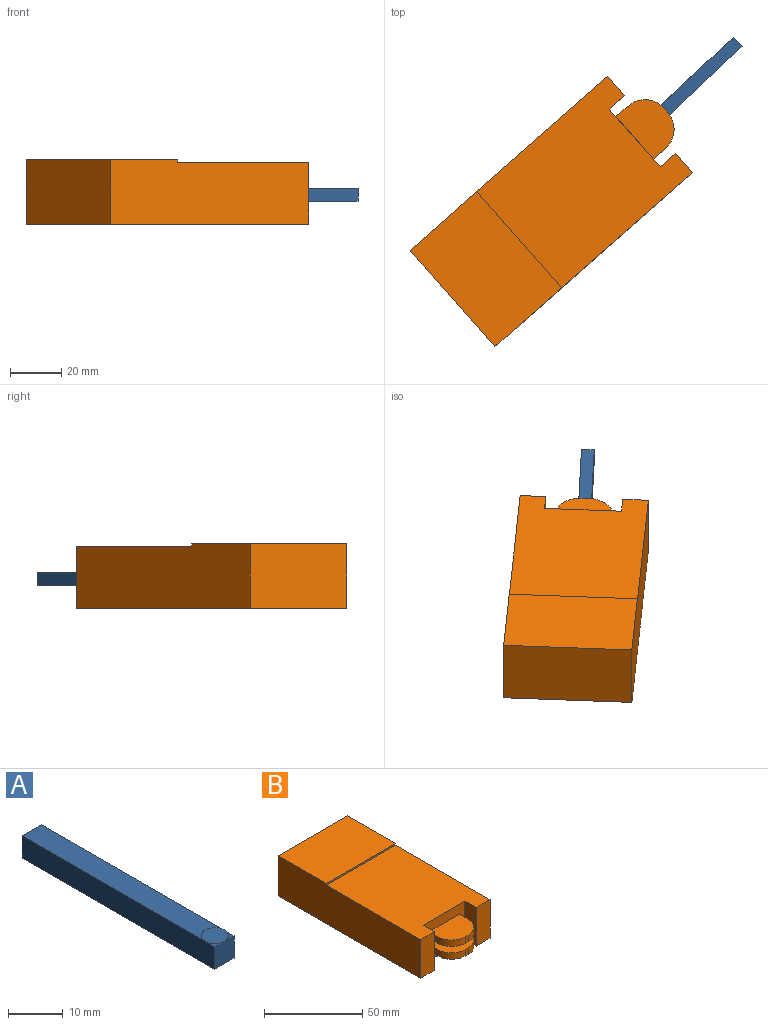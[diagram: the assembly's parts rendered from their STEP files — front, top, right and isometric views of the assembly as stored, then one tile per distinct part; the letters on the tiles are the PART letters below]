
ASSEMBLY  parts=2 mates=1
PART A: 10 faces, bbox 5x50x5.1 mm
  f0: plane 5x5mm, normal (0,1,0), area 25mm2, adj f1,f2,f3,f4
  f1: plane 50x5mm, normal (-1,0,0), area 250mm2, adj f0,f3,f4,f6,f8
  f2: plane 50x5mm, normal (1,0,0), area 250mm2, adj f0,f3,f4,f6,f7
  f3: plane 47.5x5mm, normal (0,0,1), area 227.7mm2, adj f0,f1,f2,f5
  f4: plane 50x5mm, normal (0,0,-1), area 250mm2, adj f0,f1,f2,f6
  f5: cylinder r=2.5mm len=5mm, axis (0,0,-1), area 1.6mm2, adj f3,f7,f8,f9
  f6: plane 5x5mm, normal (0,-1,0), area 25mm2, adj f1,f2,f4,f7,f8
  f7: plane 2.5x2.5mm, normal (0,0,1), area 1.3mm2, adj f2,f5,f6
  f8: plane 2.5x2.5mm, normal (0,0,1), area 1.3mm2, adj f1,f5,f6
  f9: plane 5x5mm, normal (0,0,1), area 19.6mm2, adj f5
PART B: 26 faces, bbox 50x110.8x25 mm
  f0: plane 50x1mm, normal (0,-1,0), area 50mm2, adj f1,f3,f4,f11
  f1: plane 102.55x25mm, normal (1,0,0), area 2495.7mm2, adj f0,f2,f4,f5,f9,f11
  f2: plane 50x25mm, normal (0,1,0), area 1250mm2, adj f1,f3,f4,f5
  f3: plane 102.55x25mm, normal (-1,0,0), area 2495.7mm2, adj f0,f2,f4,f5,f10,f11
  f4: plane 50x34.55mm, normal (0,0,1), area 1727.4mm2, adj f0,f1,f2,f3
  f5: plane 102.55x50mm, normal (0,0,-1), area 4887.4mm2, adj f1,f2,f3,f6,f7,f8,f9,f10
  f6: plane 24x8mm, normal (1,0,0), area 192mm2, adj f5,f7,f10,f11
  f7: plane 30x24mm, normal (0,-1,0), area 544mm2, adj f5,f6,f8,f11,f12,f13,f14,f15
  f8: plane 24x8mm, normal (-1,0,0), area 192mm2, adj f5,f7,f9,f11
  f9: plane 24x10mm, normal (0,-1,0), area 240mm2, adj f1,f5,f8,f11
  f10: plane 24x10mm, normal (0,-1,0), area 240mm2, adj f3,f5,f6,f11
  f11: plane 68x50mm, normal (0,0,1), area 3160mm2, adj f0,f1,f3,f6,f7,f8,f9,f10
  f12: plane 22x16.26mm, normal (0,0,1), area 314.9mm2, adj f7,f13,f15,f16,f22,f23
  f13: plane 6.26x4mm, normal (-1,0,0), area 25.1mm2, adj f7,f12,f14,f22
  f14: plane 22x16.26mm, normal (0,0,-1), area 314.9mm2, adj f7,f13,f15,f16,f22,f23
  f15: plane 6.26x4mm, normal (1,0,0), area 25.1mm2, adj f7,f12,f14,f23
  f16: plane 4x2mm, normal (0,-1,0), area 8mm2, adj f12,f14,f22,f23
  f17: plane 22x16.26mm, normal (0,0,1), area 314.9mm2, adj f7,f18,f20,f21,f24,f25
  f18: plane 6.26x4mm, normal (-1,0,0), area 25.1mm2, adj f7,f17,f19,f24
  f19: plane 22x16.26mm, normal (0,0,-1), area 314.9mm2, adj f7,f18,f20,f21,f24,f25
  f20: plane 6.26x4mm, normal (1,0,0), area 25.1mm2, adj f7,f17,f19,f25
  f21: plane 4x2mm, normal (0,-1,0), area 8mm2, adj f17,f19,f24,f25
  f22: cylinder r=10mm len=10mm, axis (0,0,1), area 62.8mm2, adj f12,f13,f14,f16
  f23: cylinder r=10mm len=10mm, axis (0,0,-1), area 62.8mm2, adj f12,f14,f15,f16
  f24: cylinder r=10mm len=10mm, axis (0,0,1), area 62.8mm2, adj f17,f18,f19,f21
  f25: cylinder r=10mm len=10mm, axis (0,0,-1), area 62.8mm2, adj f17,f19,f20,f21
PLACE A rot(axis=(0,0,-1),46.7deg) t=(51.54,118.01,3.84)mm
PLACE B rot(axis=(0,0,1),131.4deg) t=(14.56,34.74,-5.06)mm fixed
MATE revolute A.f5 <-> B.f14  axis (0,0,1) through (60.4,63.45,8.94)mm
